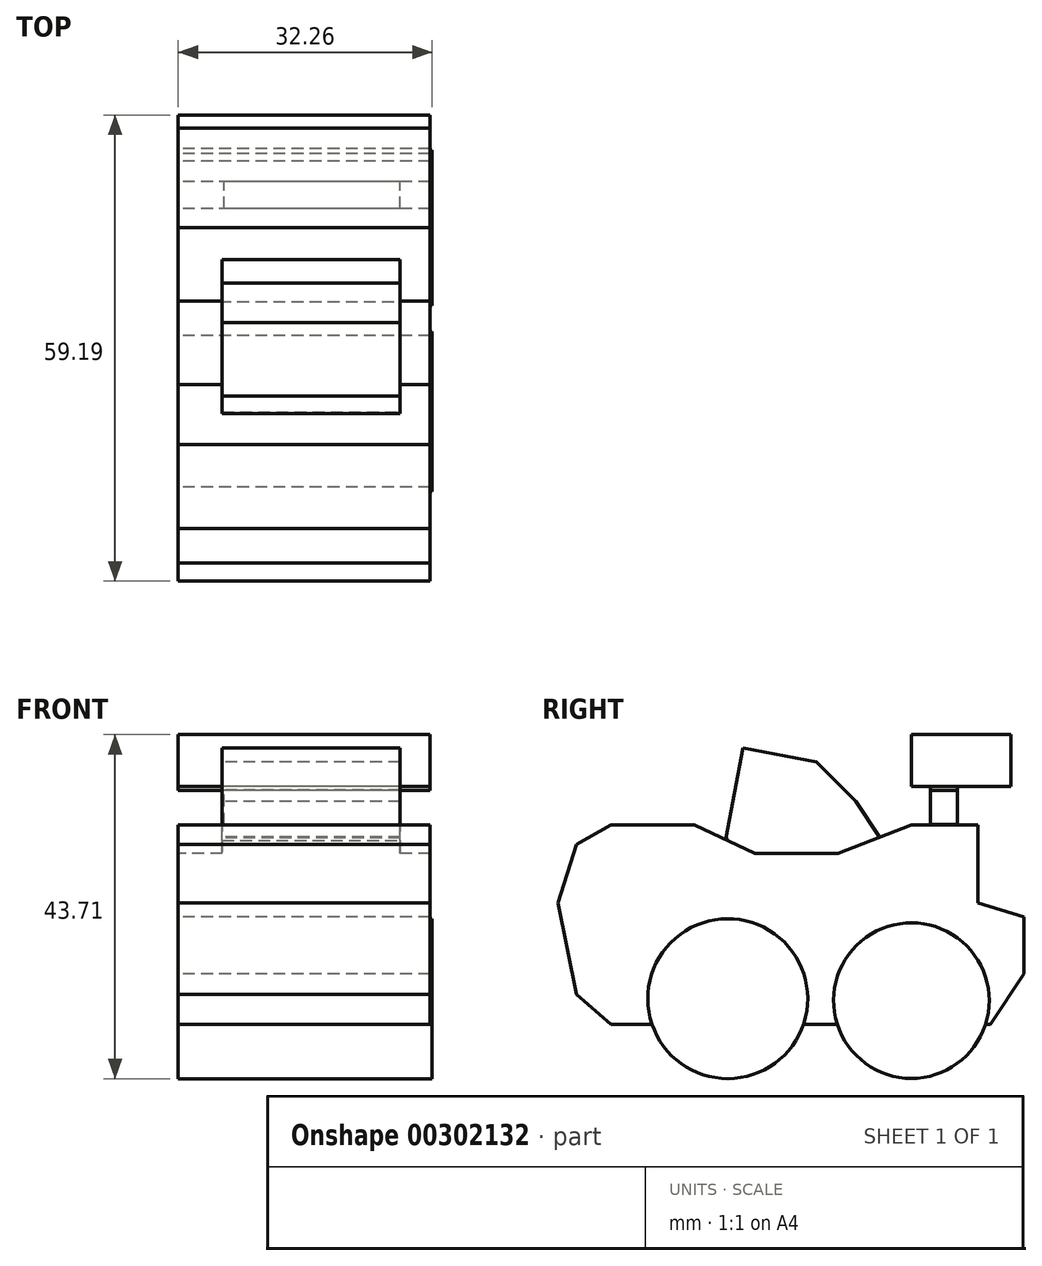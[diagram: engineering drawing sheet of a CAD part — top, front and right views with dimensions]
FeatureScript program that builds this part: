
annotation { "Feature Type Name" : "Feature", "Feature Type Description" : "" }
export const myFeature = defineFeature(function(context is Context, id is Id, definition is map)
    precondition{}
    {
        {
            var Q0;
            Q0=qCreatedBy(makeId("Right.planeOp"),FACE);
            var sketch = newSketch(context, id + "F0", { "sketchPlane" : qUnion([Q0])});
            skLineSegment(sketch, "E0", {"start": v(-30.6, -17.05) * mm, "end": v(-38.18, -17.05) * mm});
            skLineSegment(sketch, "E1", {"start": v(-38.18, -17.05) * mm, "end": v(-42.56, -13.26) * mm});
            skLineSegment(sketch, "E2", {"start": v(-42.56, -13.26) * mm, "end": v(-44.88, -1.64) * mm});
            skLineSegment(sketch, "E3", {"start": v(-44.88, -1.64) * mm, "end": v(-42.56, 5.79) * mm});
            skLineSegment(sketch, "E4", {"start": v(-42.56, 5.79) * mm, "end": v(-38.18, 8.26) * mm});
            skLineSegment(sketch, "E5", {"start": v(-38.18, 8.26) * mm, "end": v(-27.55, 8.26) * mm});
            skLineSegment(sketch, "E6", {"start": v(-27.55, 8.26) * mm, "end": v(-19.9, 4.66) * mm});
            skLineSegment(sketch, "E7", {"start": v(-19.9, 4.66) * mm, "end": v(-9.32, 4.66) * mm});
            skLineSegment(sketch, "E8", {"start": v(-9.32, 4.66) * mm, "end": v(0, 8.26) * mm});
            skLineSegment(sketch, "E9", {"start": v(0, 8.26) * mm, "end": v(8.46, 8.26) * mm});
            skLineSegment(sketch, "E10", {"start": v(8.46, 8.26) * mm, "end": v(8.46, -1.64) * mm});
            skLineSegment(sketch, "E11", {"start": v(8.46, -1.64) * mm, "end": v(14.31, -3.44) * mm});
            skLineSegment(sketch, "E12", {"start": v(14.31, -3.44) * mm, "end": v(14.31, -10.65) * mm});
            skLineSegment(sketch, "E13", {"start": v(14.31, -10.65) * mm, "end": v(10.04, -17.05) * mm});
            skLineSegment(sketch, "E14", {"start": v(10.04, -17.05) * mm, "end": v(5.3, -17.05) * mm});
            skLineSegment(sketch, "E15", {"start": v(5.3, -17.05) * mm, "end": v(5.3, -10.65) * mm});
            skLineSegment(sketch, "E16", {"start": v(5.3, -10.65) * mm, "end": v(0, -5.92) * mm});
            skLineSegment(sketch, "E17", {"start": v(0, -5.92) * mm, "end": v(-3.05, -9.35) * mm});
            skLineSegment(sketch, "E18", {"start": v(-3.05, -9.35) * mm, "end": v(-3.05, -17.05) * mm});
            skLineSegment(sketch, "E19", {"start": v(-3.05, -17.05) * mm, "end": v(-18.1, -17.05) * mm});
            skLineSegment(sketch, "E20", {"start": v(-18.1, -17.05) * mm, "end": v(-18.1, -10.65) * mm});
            skLineSegment(sketch, "E21", {"start": v(-18.1, -10.65) * mm, "end": v(-23.5, -7.5) * mm});
            skLineSegment(sketch, "E22", {"start": v(-23.5, -7.5) * mm, "end": v(-27.55, -10.65) * mm});
            skLineSegment(sketch, "E23", {"start": v(-27.55, -10.65) * mm, "end": v(-27.55, -17.05) * mm});
            skLineSegment(sketch, "E24", {"start": v(-27.55, -17.05) * mm, "end": v(-30.6, -17.05) * mm});
            skSolve(sketch);
        }
        {
            var Q0;
            Q0 = qSketchRegion(id + "F0", true);
            extrude(context, id + "F1", {"entities" : qUnion([Q0]), "depth" : 32 * mm});
        }
        {
            var Q0;
            Q0=qCreatedBy(makeId("Right.planeOp"),FACE);
            var sketch = newSketch(context, id + "F2", { "sketchPlane" : qUnion([Q0])});
            skLineSegment(sketch, "E25", {"start": v(-23.57, 6.6) * mm, "end": v(-21.38, 18.03) * mm});
            skLineSegment(sketch, "E26", {"start": v(-21.38, 18.03) * mm, "end": v(-12.06, 16.24) * mm});
            skLineSegment(sketch, "E27", {"start": v(-12.06, 16.24) * mm, "end": v(-7.04, 11.22) * mm});
            skLineSegment(sketch, "E28", {"start": v(-7.04, 11.22) * mm, "end": v(-3.63, 6.11) * mm});
            skLineSegment(sketch, "E29", {"start": v(-3.63, 6.11) * mm, "end": v(-12.06, 2.95) * mm});
            skLineSegment(sketch, "E30", {"start": v(-12.06, 2.95) * mm, "end": v(-21.38, 2.95) * mm});
            skLineSegment(sketch, "E31", {"start": v(-21.38, 2.95) * mm, "end": v(-23.57, 6.6) * mm});
            skSolve(sketch);
        }
        {
            var Q0;
            Q0 = qSketchRegion(id + "F2", true);
            extrude(context, id + "F3", {"entities" : qUnion([Q0]), "operationType" : NewBodyOperationType.ADD, "depth" : 28.2 * mm, "hasSecondDirection" : true, "secondDirectionOppositeDirection" : false, "secondDirectionDepth" : 5.6 * mm});
        }
        {
            var Q0;
            Q0=qCreatedBy(makeId("Right.planeOp"),FACE);
            var sketch = newSketch(context, id + "F4", { "sketchPlane" : qUnion([Q0])});
            skLineSegment(sketch, "E32.bottom", {"start": v(2.44, 8.3) * mm, "end": v(5.85, 8.3) * mm});
            skLineSegment(sketch, "E32.top", {"start": v(2.44, 12.68) * mm, "end": v(5.85, 12.68) * mm});
            skLineSegment(sketch, "E32.left", {"start": v(2.44, 8.3) * mm, "end": v(2.44, 12.68) * mm});
            skLineSegment(sketch, "E32.right", {"start": v(5.85, 8.3) * mm, "end": v(5.85, 12.68) * mm});
            skSolve(sketch);
        }
        {
            var Q0;
            Q0 = qSketchRegion(id + "F4", true);
            extrude(context, id + "F5", {"entities" : qUnion([Q0]), "depth" : 28.2 * mm, "hasSecondDirection" : true, "secondDirectionOppositeDirection" : false, "secondDirectionDepth" : 5.84 * mm});
        }
        {
            var Q0;
            Q0=qCreatedBy(makeId("Right.planeOp"),FACE);
            var sketch = newSketch(context, id + "F6", { "sketchPlane" : qUnion([Q0])});
            skLineSegment(sketch, "E33.bottom", {"start": v(0, 13.16) * mm, "end": v(12.65, 13.16) * mm});
            skLineSegment(sketch, "E33.top", {"start": v(0, 19.73) * mm, "end": v(12.65, 19.73) * mm});
            skLineSegment(sketch, "E33.left", {"start": v(0, 13.16) * mm, "end": v(0, 19.73) * mm});
            skLineSegment(sketch, "E33.right", {"start": v(12.65, 13.16) * mm, "end": v(12.65, 19.73) * mm});
            skSolve(sketch);
        }
        {
            var Q0;
            Q0 = qSketchRegion(id + "F6", true);
            extrude(context, id + "F7", {"entities" : qUnion([Q0]), "depth" : 32 * mm});
        }
        {
            var Q0;
            Q0=qCreatedBy(makeId("Right.planeOp"),FACE);
            var sketch = newSketch(context, id + "F8", { "sketchPlane" : qUnion([Q0])});
            skCircle(sketch, "E34", {"center": v(-23.33, -13.82) * mm, "radius": 10.16 * mm});
            skCircle(sketch, "E35", {"center": v(0, -14.06) * mm, "radius": 9.88 * mm});
            skSolve(sketch);
        }
        {
            var Q0;
            Q0 = qSketchRegion(id + "F8", true);
            extrude(context, id + "F9", {"entities" : qUnion([Q0]), "operationType" : NewBodyOperationType.ADD, "depth" : 32.26 * mm});
        }
        {
            var Q0;
            Q0=qCreatedBy(makeId("Right.planeOp"),FACE);
            var sketch = newSketch(context, id + "F10", { "sketchPlane" : qUnion([Q0])});
            skLineSegment(sketch, "E36.bottom", {"start": v(2.44, 12.66) * mm, "end": v(5.87, 12.66) * mm});
            skLineSegment(sketch, "E36.top", {"start": v(2.44, 13.17) * mm, "end": v(5.87, 13.17) * mm});
            skLineSegment(sketch, "E36.left", {"start": v(2.44, 12.66) * mm, "end": v(2.44, 13.17) * mm});
            skLineSegment(sketch, "E36.right", {"start": v(5.87, 12.66) * mm, "end": v(5.87, 13.17) * mm});
            skSolve(sketch);
        }
        {
            var Q0;
            Q0 = qSketchRegion(id + "F10", true);
            extrude(context, id + "F11", {"entities" : qUnion([Q0]), "depth" : 32 * mm});
        }
    });
